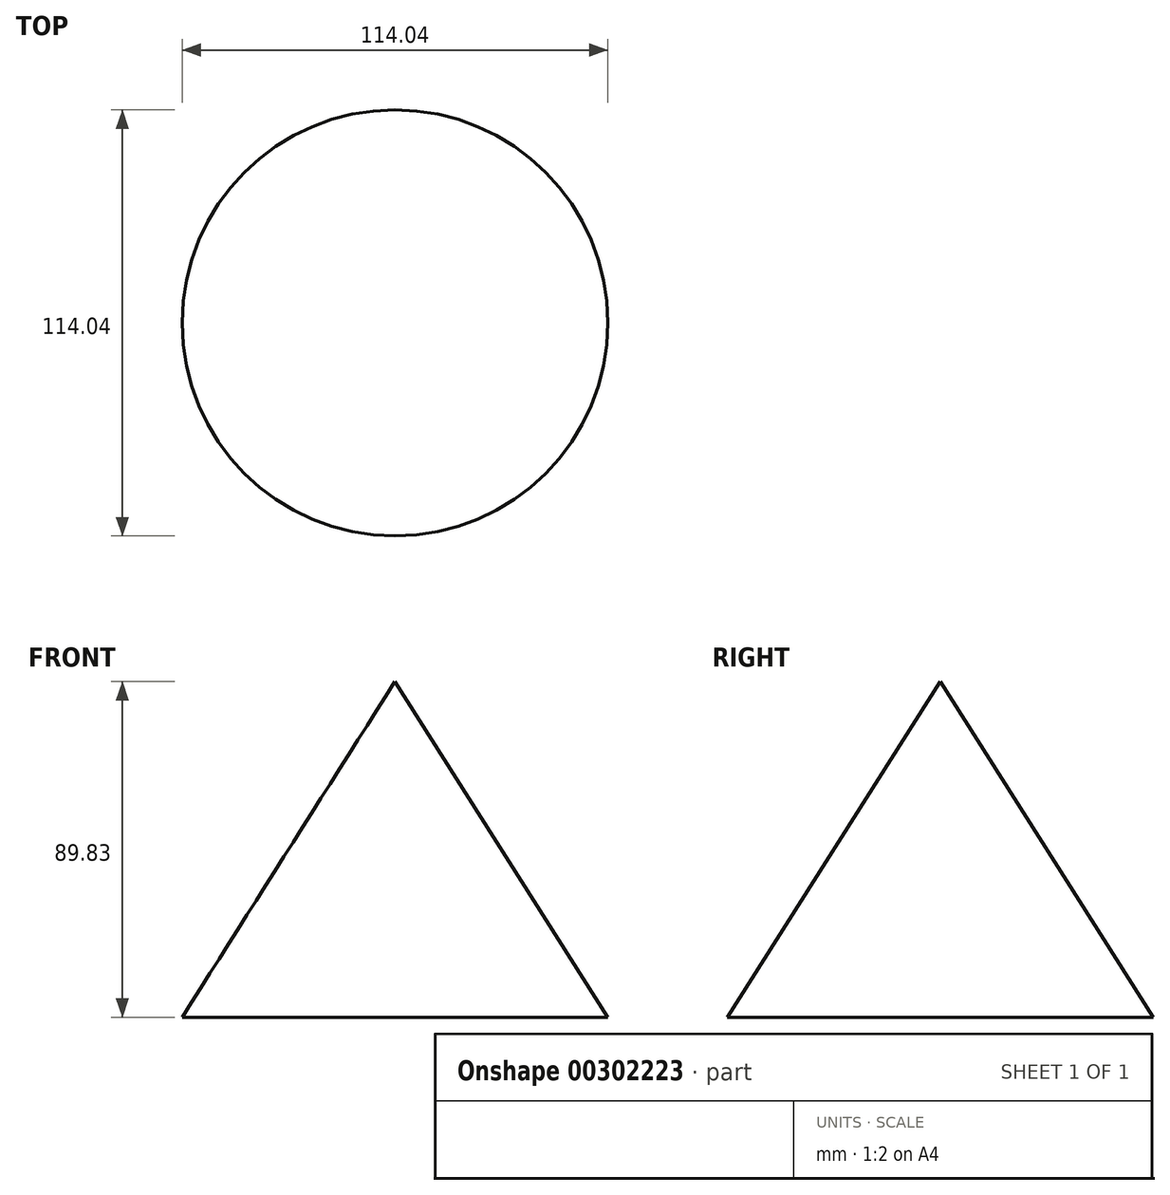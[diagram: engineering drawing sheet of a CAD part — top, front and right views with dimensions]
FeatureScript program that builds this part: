
annotation { "Feature Type Name" : "Feature", "Feature Type Description" : "" }
export const myFeature = defineFeature(function(context is Context, id is Id, definition is map)
    precondition{}
    {
        {
            var Q0;
            Q0=qCreatedBy(makeId("Front.planeOp"),FACE);
            var sketch = newSketch(context, id + "F0", { "sketchPlane" : qUnion([Q0])});
            skLineSegment(sketch, "E0", {"start": v(0, -38.7) * mm, "end": v(57.02, -38.7) * mm});
            skLineSegment(sketch, "E1", {"start": v(57.02, -38.7) * mm, "end": v(0, 51.13) * mm});
            skPoint(sketch, "E2", {"position": v(0, -38.7) * mm});
            skLineSegment(sketch, "E3", {"start": v(0, 51.13) * mm, "end": v(0, -38.7) * mm});
            skSolve(sketch);
        }
        {
            var Q0;
            Q0=makeQuery(id+"F0.imprint","IMPRINT",FACE,{"disambiguationData":[TD([[makeQuery(id+"F0.imprint","IMPRINT",EDGE,{"derivedFrom":sQuery(id+"F0.wireOp",EDGE,"E0")}),1.0]])]});
            var Q1;
            Q1=sQuery(id+"F0.wireOp",EDGE,"E3");
            revolve(context, id + "F1", {"entities" : qUnion([Q0]), "axis" : qUnion([Q1]), "revolveType" : RevolveType.FULL});
        }
    });
